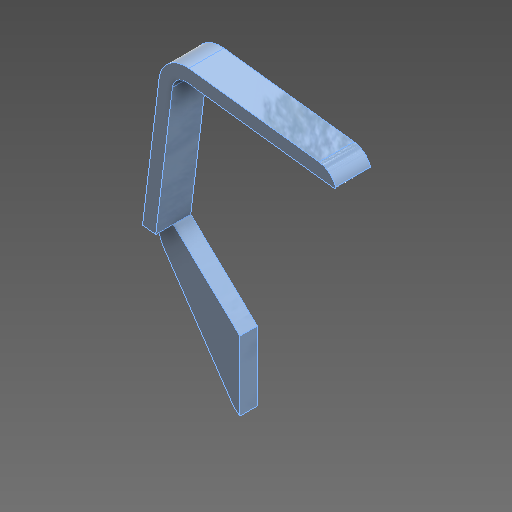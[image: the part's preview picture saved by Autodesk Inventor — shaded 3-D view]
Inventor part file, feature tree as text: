
AUTODESK INVENTOR PART (.ipt)
format: ipt  version: 2020 (Build 240168000, 168)  size: 170,496 bytes
history: native  units: in
note: dims shown in document units (in); Inventor stores cm internally (conversion verified against a paired STEP export)
features: fillet x3, extrude x2, other x1
ambient origin geometry x8: Origin, YZ Plane, XZ Plane, XY Plane, X Axis, Y Axis, Z Axis, Center Point
bodies: Body1 (feature_tree)
feature tree (6):
  other  "Base Sketch"
  extrude  "Lower Arm"  Depth=0.8661in
  extrude  "Upper Arm"  Depth=0.2067in
  fillet  "Fillet1"  [1 undecoded]
  fillet  "Fillet3"  Radius=0.4134in
  fillet  "Fillet4"  [1 undecoded]
note: 2 required parameter values undecoded (feature->parameter linkage not recoverable at this tier; creation-order binding heuristic only, values carry confidence <= 0.55)
